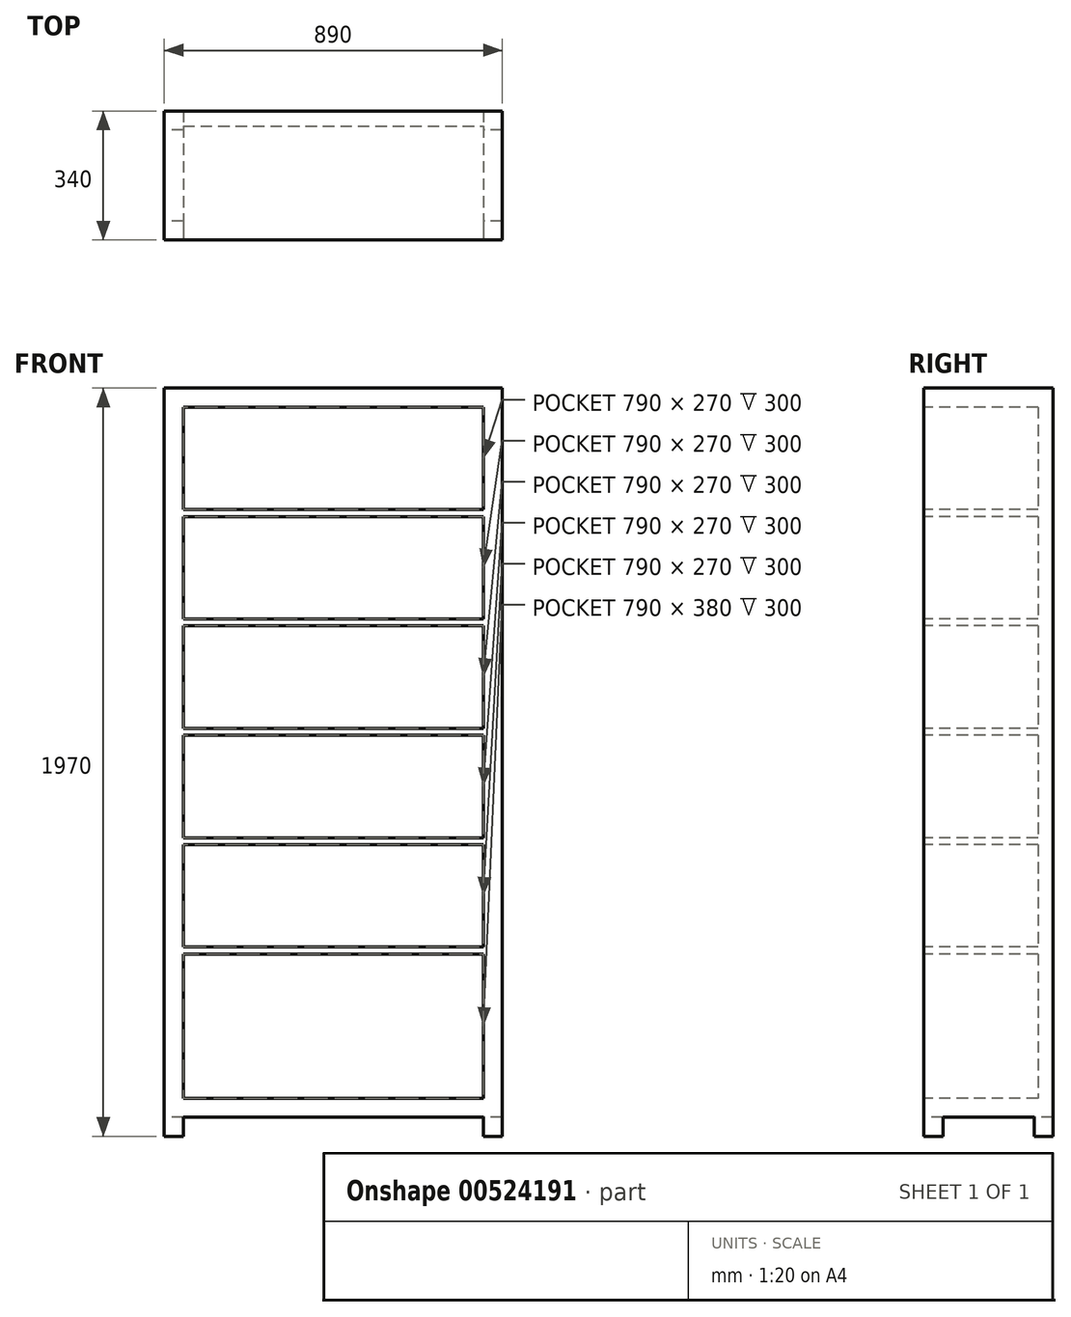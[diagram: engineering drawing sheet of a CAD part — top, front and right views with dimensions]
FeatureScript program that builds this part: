
annotation { "Feature Type Name" : "Feature", "Feature Type Description" : "" }
export const myFeature = defineFeature(function(context is Context, id is Id, definition is map)
    precondition{}
    {
        {
            var Q0;
            Q0=qCreatedBy(makeId("Top.planeOp"),FACE);
            var sketch = newSketch(context, id + "F0", { "sketchPlane" : qUnion([Q0])});
            skLineSegment(sketch, "E0.bottom", {"start": v(0, 0) * mm, "end": v(-890, 0) * mm});
            skLineSegment(sketch, "E0.top", {"start": v(0, 340) * mm, "end": v(-890, 340) * mm});
            skLineSegment(sketch, "E0.left", {"start": v(0, 0) * mm, "end": v(0, 340) * mm});
            skLineSegment(sketch, "E0.right", {"start": v(-890, 0) * mm, "end": v(-890, 340) * mm});
            skSolve(sketch);
        }
        {
            var Q0;
            Q0 = qSketchRegion(id + "F0", true);
            extrude(context, id + "F1", {"entities" : qUnion([Q0]), "depth" : 1970 * mm, "offsetDistance" : 25 * mm});
        }
        {
            var Q0;
            Q0=makeQuery(id+"F1.opExtrude","SWEPT_FACE",FACE,{"disambiguationData":[OSD([sQuery(id+"F0.wireOp",EDGE,"E0.bottom")])]});
            var sketch = newSketch(context, id + "F2", { "sketchPlane" : qUnion([Q0])});
            skLineSegment(sketch, "E1.0", {"start": v(-890, 1970) * mm, "end": v(-890, 0) * mm});
            skLineSegment(sketch, "E2.0", {"start": v(0, 0) * mm, "end": v(-890, 0) * mm});
            skLineSegment(sketch, "E3.0", {"start": v(0, 1970) * mm, "end": v(0, 0) * mm});
            skLineSegment(sketch, "E4.0", {"start": v(0, 1970) * mm, "end": v(-890, 1970) * mm});
            skLineSegment(sketch, "E5.bottom", {"start": v(-840, 1920) * mm, "end": v(-50, 1920) * mm});
            skLineSegment(sketch, "E5.top", {"start": v(-840, 100) * mm, "end": v(-50, 100) * mm});
            skLineSegment(sketch, "E5.left", {"start": v(-840, 1920) * mm, "end": v(-840, 100) * mm});
            skLineSegment(sketch, "E5.right", {"start": v(-50, 1920) * mm, "end": v(-50, 100) * mm});
            skLineSegment(sketch, "E6.bottom", {"start": v(-840, 50) * mm, "end": v(-50, 50) * mm});
            skLineSegment(sketch, "E6.top", {"start": v(-840, 0) * mm, "end": v(-50, 0) * mm});
            skLineSegment(sketch, "E6.left", {"start": v(-840, 50) * mm, "end": v(-840, 0) * mm});
            skLineSegment(sketch, "E6.right", {"start": v(-50, 50) * mm, "end": v(-50, 0) * mm});
            skLineSegment(sketch, "E7.bottom", {"start": v(-840, 1650) * mm, "end": v(-50, 1650) * mm});
            skLineSegment(sketch, "E7.top", {"start": v(-840, 1632) * mm, "end": v(-50, 1632) * mm});
            skLineSegment(sketch, "E7.left", {"start": v(-840, 1650) * mm, "end": v(-840, 1632) * mm});
            skLineSegment(sketch, "E7.right", {"start": v(-50, 1650) * mm, "end": v(-50, 1632) * mm});
            skLineSegment(sketch, "E8.bottom", {"start": v(-840, 1362) * mm, "end": v(-50, 1362) * mm});
            skLineSegment(sketch, "E8.top", {"start": v(-840, 1344) * mm, "end": v(-50, 1344) * mm});
            skLineSegment(sketch, "E8.left", {"start": v(-840, 1362) * mm, "end": v(-840, 1344) * mm});
            skLineSegment(sketch, "E8.right", {"start": v(-50, 1362) * mm, "end": v(-50, 1344) * mm});
            skLineSegment(sketch, "E9.bottom", {"start": v(-840, 1074) * mm, "end": v(-50, 1074) * mm});
            skLineSegment(sketch, "E9.top", {"start": v(-840, 1056) * mm, "end": v(-50, 1056) * mm});
            skLineSegment(sketch, "E9.left", {"start": v(-840, 1074) * mm, "end": v(-840, 1056) * mm});
            skLineSegment(sketch, "E9.right", {"start": v(-50, 1074) * mm, "end": v(-50, 1056) * mm});
            skLineSegment(sketch, "E10.bottom", {"start": v(-840, 786) * mm, "end": v(-50, 786) * mm});
            skLineSegment(sketch, "E10.top", {"start": v(-840, 768) * mm, "end": v(-50, 768) * mm});
            skLineSegment(sketch, "E10.left", {"start": v(-840, 786) * mm, "end": v(-840, 768) * mm});
            skLineSegment(sketch, "E10.right", {"start": v(-50, 786) * mm, "end": v(-50, 768) * mm});
            skLineSegment(sketch, "E11.bottom", {"start": v(-840, 498) * mm, "end": v(-50, 498) * mm});
            skLineSegment(sketch, "E11.top", {"start": v(-840, 480) * mm, "end": v(-50, 480) * mm});
            skLineSegment(sketch, "E11.left", {"start": v(-840, 498) * mm, "end": v(-840, 480) * mm});
            skLineSegment(sketch, "E11.right", {"start": v(-50, 498) * mm, "end": v(-50, 480) * mm});
            skSolve(sketch);
        }
        {
            var Q0;
            Q0=makeQuery(id+"F2.imprint","IMPRINT",FACE,{"disambiguationData":[TD([[makeQuery(id+"F2.imprint","IMPRINT",EDGE,{"derivedFrom":sQuery(id+"F2.wireOp",EDGE,"E6.bottom")}),-1.0]])]});
            extrude(context, id + "F3", {"entities" : qUnion([Q0]), "operationType" : NewBodyOperationType.REMOVE, "oppositeDirection" : true, "depth" : 350 * mm, "offsetDistance" : 25 * mm});
        }
        {
            var Q0;
            {var subQ0=sQuery(id+"F2.wireOp",EDGE,"E5.top");Q0=makeQuery(id+"F2.imprint","IMPRINT",FACE,{"disambiguationData":[TD([[makeQuery(id+"F2.imprint","IMPRINT",EDGE,{"derivedFrom":subQ0}),1.0]])]});}
            var Q1;
            {var subQ0=sQuery(id+"F2.wireOp",EDGE,"E10.top");Q1=makeQuery(id+"F2.imprint","IMPRINT",FACE,{"disambiguationData":[TD([[makeQuery(id+"F2.imprint","IMPRINT",EDGE,{"derivedFrom":subQ0}),-1.0]])]});}
            var Q2;
            {var subQ0=sQuery(id+"F2.wireOp",EDGE,"E9.top");Q2=makeQuery(id+"F2.imprint","IMPRINT",FACE,{"disambiguationData":[TD([[makeQuery(id+"F2.imprint","IMPRINT",EDGE,{"derivedFrom":subQ0}),-1.0]])]});}
            var Q3;
            {var subQ0=sQuery(id+"F2.wireOp",EDGE,"E8.top");Q3=makeQuery(id+"F2.imprint","IMPRINT",FACE,{"disambiguationData":[TD([[makeQuery(id+"F2.imprint","IMPRINT",EDGE,{"derivedFrom":subQ0}),-1.0]])]});}
            var Q4;
            {var subQ0=sQuery(id+"F2.wireOp",EDGE,"E7.top");Q4=makeQuery(id+"F2.imprint","IMPRINT",FACE,{"disambiguationData":[TD([[makeQuery(id+"F2.imprint","IMPRINT",EDGE,{"derivedFrom":subQ0}),-1.0]])]});}
            var Q5;
            {var subQ0=sQuery(id+"F2.wireOp",EDGE,"E5.bottom");Q5=makeQuery(id+"F2.imprint","IMPRINT",FACE,{"disambiguationData":[TD([[makeQuery(id+"F2.imprint","IMPRINT",EDGE,{"derivedFrom":subQ0}),-1.0]])]});}
            extrude(context, id + "F4", {"entities" : qUnion([Q0, Q1, Q2, Q3, Q4, Q5]), "operationType" : NewBodyOperationType.REMOVE, "oppositeDirection" : true, "depth" : 300 * mm, "offsetDistance" : 25 * mm});
        }
        {
            var Q0;
            Q0=makeQuery(id+"F1.opExtrude","SWEPT_FACE",FACE,{"disambiguationData":[OSD([sQuery(id+"F0.wireOp",EDGE,"E0.right")])]});
            var sketch = newSketch(context, id + "F5", { "sketchPlane" : qUnion([Q0])});
            skLineSegment(sketch, "E12.0", {"start": v(-340, 1970) * mm, "end": v(-340, 0) * mm});
            skLineSegment(sketch, "E13.0", {"start": v(0, 0) * mm, "end": v(-340, 0) * mm});
            skLineSegment(sketch, "E14.0", {"start": v(0, 1920) * mm, "end": v(0, 100) * mm});
            skLineSegment(sketch, "E15.bottom", {"start": v(-290, 0) * mm, "end": v(-50, 0) * mm});
            skLineSegment(sketch, "E15.top", {"start": v(-290, 50) * mm, "end": v(-50, 50) * mm});
            skLineSegment(sketch, "E15.left", {"start": v(-290, 0) * mm, "end": v(-290, 50) * mm});
            skLineSegment(sketch, "E15.right", {"start": v(-50, 0) * mm, "end": v(-50, 50) * mm});
            skSolve(sketch);
        }
        {
            var Q0;
            Q0=makeQuery(id+"F5.imprint","IMPRINT",FACE,{"disambiguationData":[TD([[makeQuery(id+"F5.imprint","IMPRINT",EDGE,{"derivedFrom":sQuery(id+"F5.wireOp",EDGE,"E15.top")}),-1.0]])]});
            extrude(context, id + "F6", {"entities" : qUnion([Q0]), "operationType" : NewBodyOperationType.REMOVE, "oppositeDirection" : true, "depth" : 895 * mm, "offsetDistance" : 25 * mm});
        }
    });
